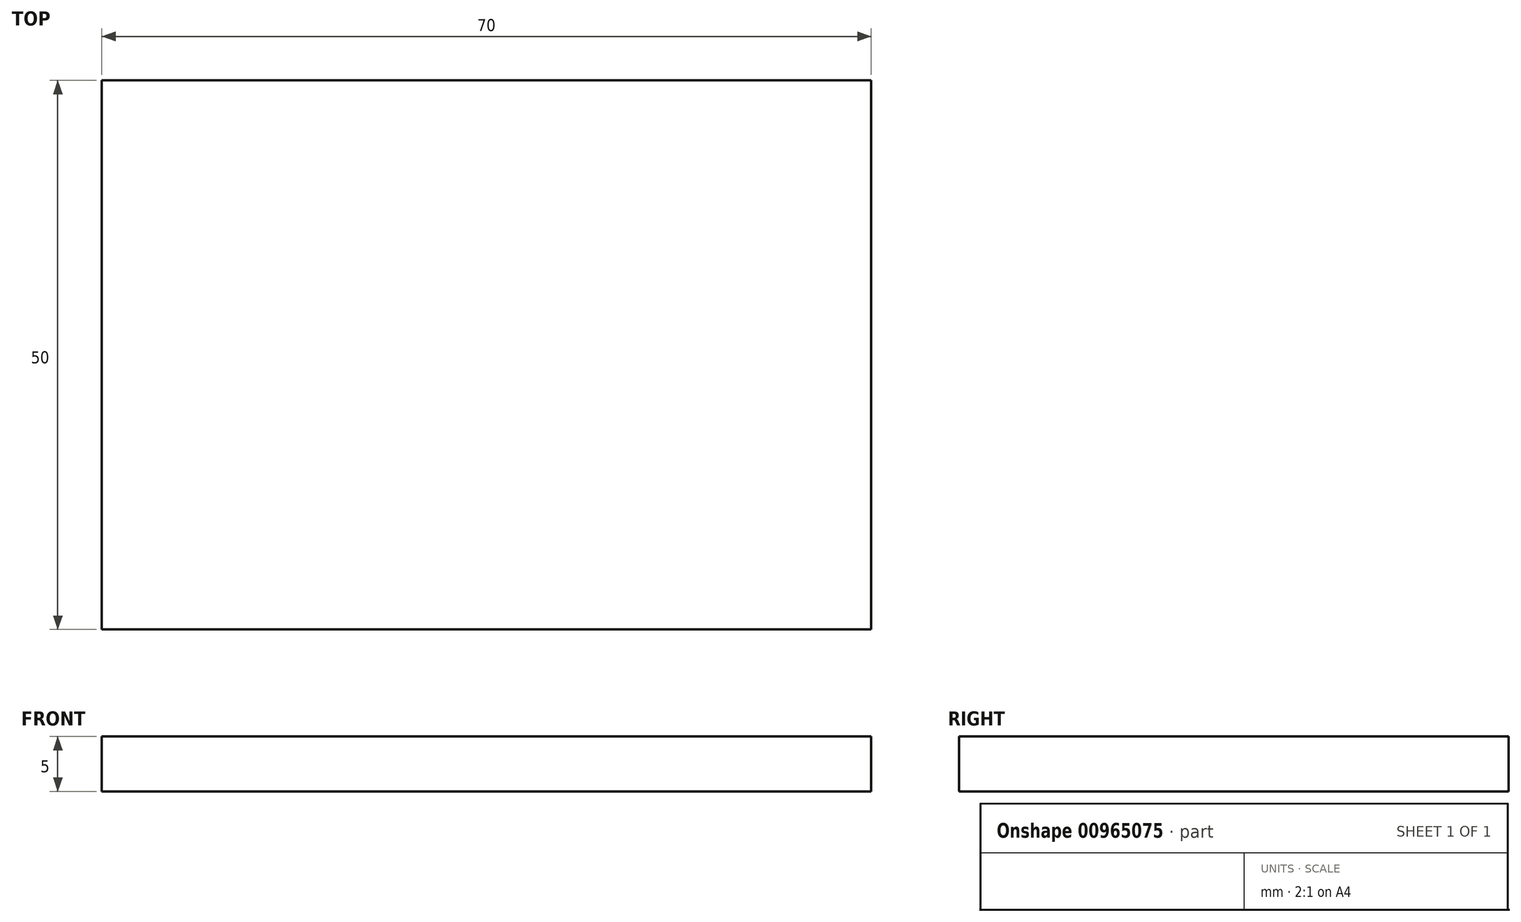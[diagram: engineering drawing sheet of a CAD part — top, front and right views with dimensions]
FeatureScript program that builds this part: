
annotation { "Feature Type Name" : "Feature", "Feature Type Description" : "" }
export const myFeature = defineFeature(function(context is Context, id is Id, definition is map)
    precondition{}
    {
        {
            var Q0;
            Q0=qCreatedBy(makeId("Top.planeOp"),FACE);
            var sketch = newSketch(context, id + "F0", { "sketchPlane" : qUnion([Q0])});
            skLineSegment(sketch, "E0.bottom", {"start": v(0, 0) * mm, "end": v(70, 0) * mm});
            skLineSegment(sketch, "E0.top", {"start": v(0, 50) * mm, "end": v(70, 50) * mm});
            skLineSegment(sketch, "E0.left", {"start": v(0, 0) * mm, "end": v(0, 50) * mm});
            skLineSegment(sketch, "E0.right", {"start": v(70, 0) * mm, "end": v(70, 50) * mm});
            skSolve(sketch);
        }
        {
            var Q0;
            Q0=makeQuery(id+"F0.imprint","IMPRINT",FACE,{"disambiguationData":[TD([[makeQuery(id+"F0.imprint","IMPRINT",EDGE,{"derivedFrom":sQuery(id+"F0.wireOp",EDGE,"E0.bottom")}),1.0]])]});
            extrude(context, id + "F1", {"entities" : qUnion([Q0]), "depth" : 5 * mm, "offsetDistance" : 25 * mm});
        }
    });
